# Revit family: QF_BPRO_RWR-B 6 x 4_575104
name_source: partatom
category: Sonderausstattung
revit_build: Autodesk Revit 2018 (Build: 20181015_0930(x64)
units: mm (PartAtom-declared; Revit-internal decimal feet)

## family parameters
Arbeitsebenenbasiert = Nein
Beim Laden mit Abzugskörper schneiden = Nein
Bemaßung runder Anschluss = Durchmesser verwenden
Gemeinsam genutzt = Nein
Immer vertikal = Ja
Raumberechnungspunkt = Nein
Teiletyp = Normal

## types (1)
- RWR-B 6 x 4
    Artikel Nummer = 575104
    Beschreibung = Regalwagen,
zum Transport
von Backblechen
600 x 400 mm
    Beschreibung durch Hersteller analog Leistungsverzeichnislangtext = Abmessungen

Länge:			686 mm
Breite:		536 mm
Höhe:		1729 mm

Lichtes Maß:
Abstand der Auflagenschienen:	    73 mm


Ausführung

Der Regalwagen besteht aus CNS 18/10, Werkstoff-Nr. 1.4301. Zwischen stabilem Vierkant-rohr mit 25 x 25 mm (gebogen ohne Einzug) befinden sich eingeschweißte Führungsschienen. Diese sind mit einer beidseitigen Durchschubsicherung zum Längseinschub von Backblechen 60x40 cm vorgesehen.
Ein eingeschweißtes Vierkantrohr 20 x 10 mm auf mittlerer Höhe des Regalwagens, jeweils an Vorder- und Rückseite höhenversetzt angebracht, verstärkt zusätzlich die Stabilität.

Der Regalwagen ist fahrbar mittels rostfreien Kunststoffrollen gemäß DIN 18867, Teil 8
(4 Lenkrollen, davon 2 mit Feststeller, Rollendurchmesser 125 mm). Wandabweiser aus Kunststoff (Polyamid) an allen vier Ecken schützen vor Beschädigung.



Technische Daten

Werkstoff:	 	Chromnickelstahl 18/10,
	 	Polyamid (PA)
Materialstärke VK-Rohr:	1,5 mm
Materialstärke
Auflageschienen:		    1,25 mm
Gewicht:		21,5 kg
Tragfähigkeit je Wagen:	    200 kg
Anzahl Auflagenpaare:		20
Kapazität:		20 Backbleche 60x40 cm




Besonderheit

•	Führungsschienen mit beidseitiger Durchschubsicherung


Fabrikat

Hersteller:		B.PRO
Typ:                                    RWR-B 6x4-20
Best.Nr.		575 104
    CE Kennzeichnung = Ja
    Gerätegewicht Netto = 21.50 kg
    Großküchengerätezuordnung = Ja
    Hersteller = B.PRO GmbH
    Höhe = 1729 mm  [stored 5.67257 ft]
    Internetadresse Gerätehersteller = https://www.bpro-solutions.com
    Kosten = 843.5 $
    Länge Gerätebreite = 686 mm
    Material = QF_Metal-Stainless-Steel_general
    Material Rollen = QF_Plastic-Dark_Grey-Matt
    Material Stoßschutz = QF_Plastic-Dark_Grey-Matt
    Modell = RWR-B 6 x 4
    Tiefe = 536 mm
    Typenkommentare = Regalwagen
    URL = https://www.bpro-solutions.com
    Warnhinweise = Der Regalwagen darf nicht zum Transport von Personen mit oder auf dem Wagen benutzt werden. Der Regalwagen darf nicht als "Leiterersatz" oder als Klettergerät (Kinder) benutzt werden (Kippgefahr). Für diese Anwendungsfälle oder sonstigen, nicht bestimmungsgemäßen Gebrauch erlischt die Gewährleistung.
Ausführliche Gefahrenhinweise entnehmen Sie der Betriebsanleitung.
    Zubehör = Ja

note: [stored X ft] marks values corroborated as IEEE doubles in the binary element streams (Revit-internal decimal feet)
